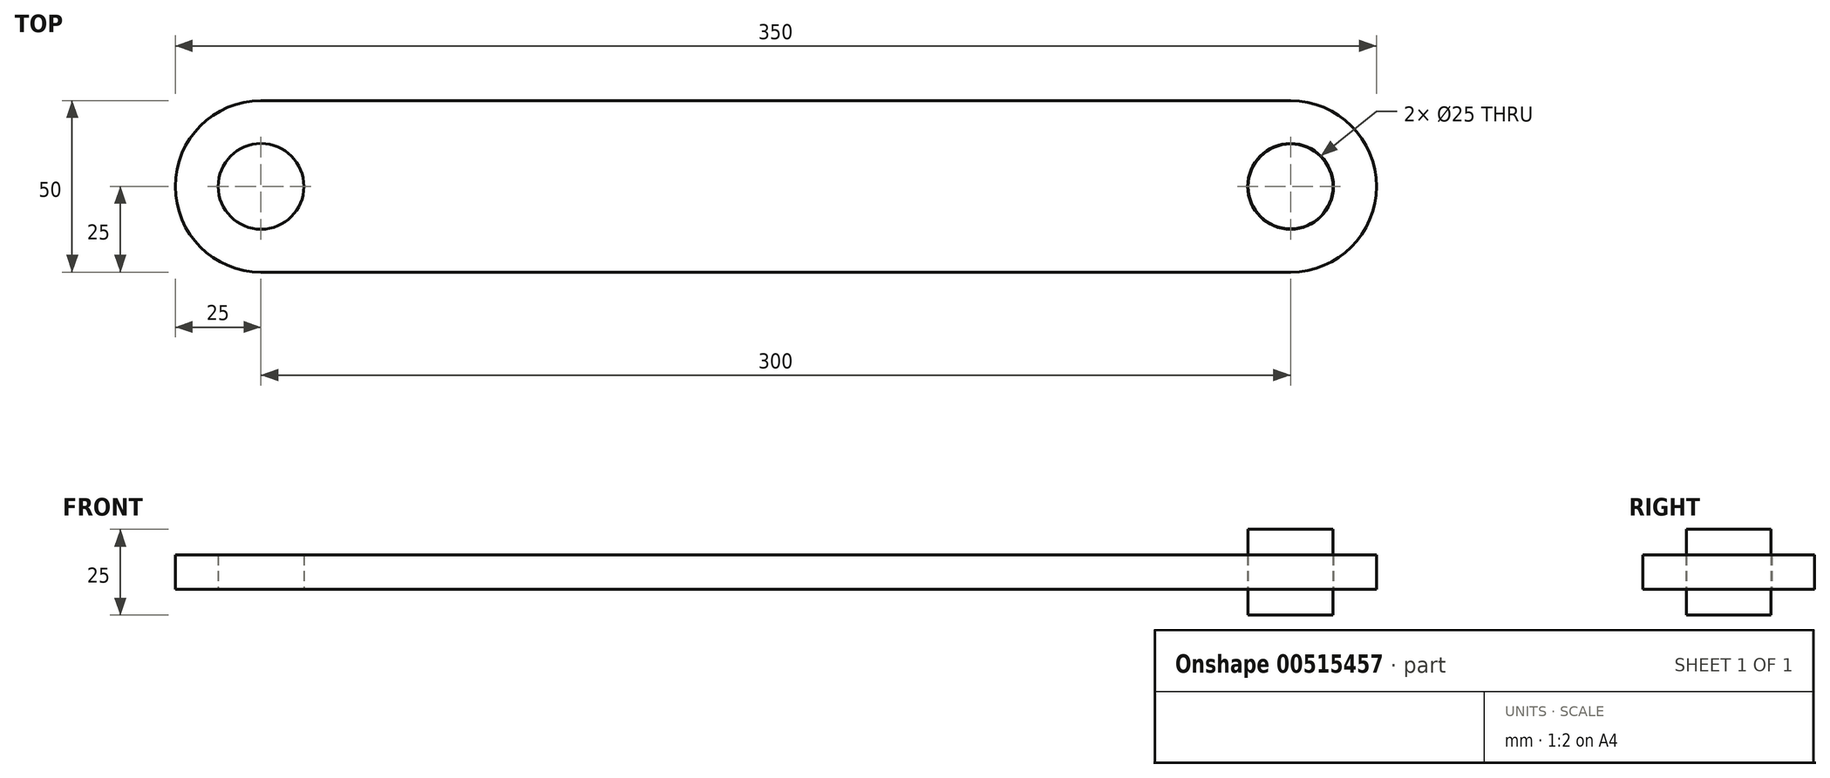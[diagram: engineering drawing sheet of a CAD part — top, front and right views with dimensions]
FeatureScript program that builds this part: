
annotation { "Feature Type Name" : "Feature", "Feature Type Description" : "" }
export const myFeature = defineFeature(function(context is Context, id is Id, definition is map)
    precondition{}
    {
        {
            var Q0;
            Q0=qCreatedBy(makeId("Top.planeOp"),FACE);
            var sketch = newSketch(context, id + "F0", { "sketchPlane" : qUnion([Q0])});
            skLineSegment(sketch, "E0.bottom", {"start": v(150, 25) * mm, "end": v(-150, 25) * mm});
            skLineSegment(sketch, "E0.top", {"start": v(150, -25) * mm, "end": v(-150, -25) * mm});
            skPoint(sketch, "E0.middle", {"position": v(0, 0) * mm});
            skArc(sketch, "E1", {"start": v(150, 25) * mm, "mid": v(175, 0) * mm, "end": v(150, -25) * mm});
            skArc(sketch, "E2", {"start": v(-150, 25) * mm, "mid": v(-175, 0) * mm, "end": v(-150, -25) * mm});
            skCircle(sketch, "E3", {"center": v(-150, 0) * mm, "radius": 12.5 * mm});
            skCircle(sketch, "E4", {"center": v(150, 0) * mm, "radius": 12.5 * mm});
            skSolve(sketch);
        }
        {
            var Q0;
            Q0 = qSketchRegion(id + "F0", true);
            extrude(context, id + "F1", {"entities" : qUnion([Q0]), "endBound" : BoundingType.SYMMETRIC, "depth" : 10 * mm, "offsetDistance" : 25.4 * mm});
        }
        {
            var Q0;
            Q0=qCreatedBy(makeId("Top.planeOp"),FACE);
            var sketch = newSketch(context, id + "F2", { "sketchPlane" : qUnion([Q0])});
            skCircle(sketch, "E5", {"center": v(150, 0) * mm, "radius": 12.37 * mm});
            skSolve(sketch);
        }
        {
            var Q0;
            Q0 = qSketchRegion(id + "F2", true);
            extrude(context, id + "F3", {"entities" : qUnion([Q0]), "endBound" : BoundingType.SYMMETRIC, "depth" : 25 * mm, "offsetDistance" : 25 * mm});
        }
    });
